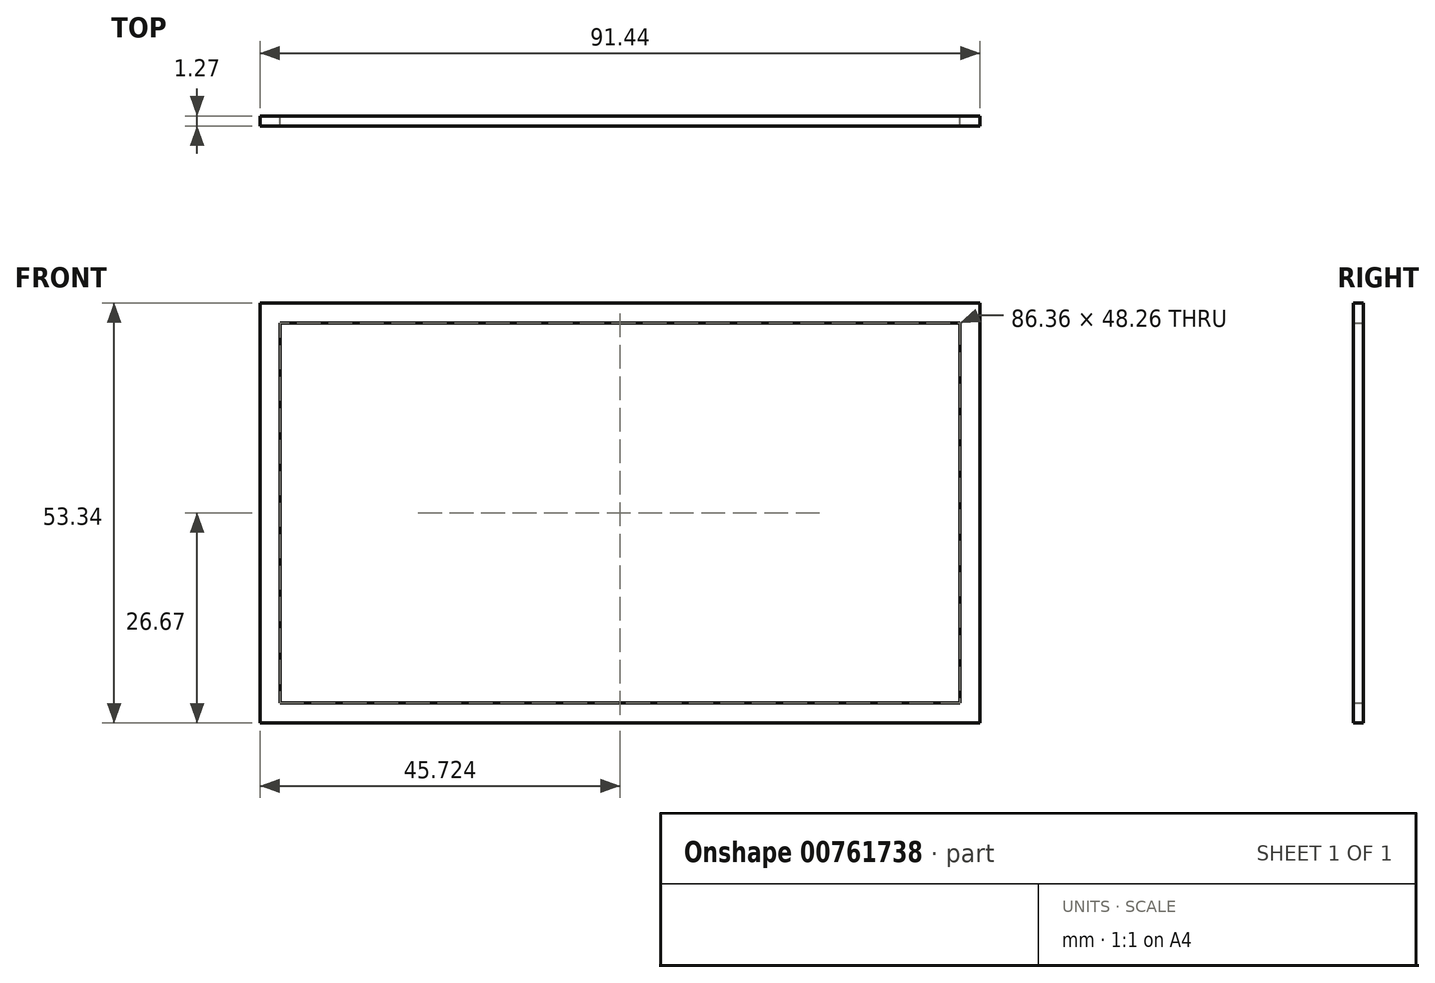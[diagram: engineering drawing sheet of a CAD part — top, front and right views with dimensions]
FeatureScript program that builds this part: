
annotation { "Feature Type Name" : "Feature", "Feature Type Description" : "" }
export const myFeature = defineFeature(function(context is Context, id is Id, definition is map)
    precondition{}
    {
        {
            var Q0;
            Q0=qCreatedBy(makeId("Front.planeOp"),FACE);
            var sketch = newSketch(context, id + "F0", { "sketchPlane" : qUnion([Q0])});
            skLineSegment(sketch, "E0.bottom", {"start": v(-46.5, 13.65) * mm, "end": v(44.93, 13.65) * mm});
            skLineSegment(sketch, "E0.top", {"start": v(-46.5, -39.7) * mm, "end": v(44.93, -39.7) * mm});
            skLineSegment(sketch, "E0.left", {"start": v(-46.5, 13.65) * mm, "end": v(-46.5, -39.7) * mm});
            skLineSegment(sketch, "E0.right", {"start": v(44.93, 13.65) * mm, "end": v(44.93, -39.7) * mm});
            skSolve(sketch);
        }
        {
            var Q0;
            Q0=makeQuery(id+"F0.imprint","IMPRINT",FACE,{"disambiguationData":[TD([[makeQuery(id+"F0.imprint","IMPRINT",EDGE,{"derivedFrom":sQuery(id+"F0.wireOp",EDGE,"E0.bottom")}),-1.0]])]});
            extrude(context, id + "F1", {"entities" : qUnion([Q0]), "depth" : 1.27 * mm, "offsetDistance" : 25.4 * mm});
        }
        {
            var Q0;
            Q0=makeQuery(id+"F1.opExtrude","CAP_FACE",FACE,{"disambiguationData":[OSD([sQuery(id+"F0.wireOp",EDGE,"E0.bottom"),sQuery(id+"F0.wireOp",EDGE,"E0.top"),sQuery(id+"F0.wireOp",EDGE,"E0.left"),sQuery(id+"F0.wireOp",EDGE,"E0.right")])],"isStart":false});
            var Q1;
            Q1=makeQuery(id+"F1.opExtrude","CAP_FACE",FACE,{"disambiguationData":[OSD([sQuery(id+"F0.wireOp",EDGE,"E0.bottom"),sQuery(id+"F0.wireOp",EDGE,"E0.top"),sQuery(id+"F0.wireOp",EDGE,"E0.left"),sQuery(id+"F0.wireOp",EDGE,"E0.right")])],"isStart":true});
            shell(context, id + "F2", {"entities" : qUnion([Q0, Q1]), "thickness" : 2.54 * mm});
        }
    });
